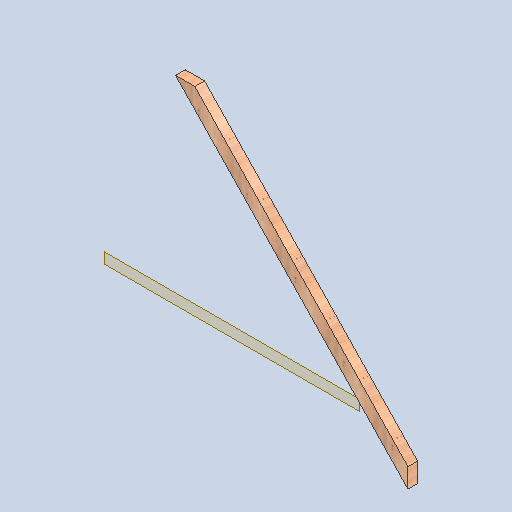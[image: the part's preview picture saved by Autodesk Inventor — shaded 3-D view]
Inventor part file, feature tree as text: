
AUTODESK INVENTOR PART (.ipt)
format: ipt  version: 2025 (Build 290162000, 162)  size: 152,064 bytes
history: native  units: in
note: dims shown in document units (in); Inventor stores cm internally (conversion verified against a paired STEP export)
features: other x3, sketch x1, plane x1
ambient origin geometry x8: Origin, YZ Plane, XZ Plane, XY Plane, X Axis, Y Axis, Z Axis, Center Point
bodies: Solid1 (feature_tree)
feature tree (5):
  other  "leg slant.ipt"
  other  "Solid3::leg slant.ipt"
  other  "TaggingFeature1"
  sketch  "Sketch1"  dims[d0=0.3937in]
  plane  "Work Plane1"
